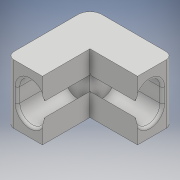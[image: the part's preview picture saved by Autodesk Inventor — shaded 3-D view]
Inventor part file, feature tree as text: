
AUTODESK INVENTOR PART (.ipt)
format: ipt  version: 2017 (Build 210142000, 142)  size: 176,640 bytes
history: native  units: mm
features: extrude x3, fillet x3, sketch x3
ambient origin geometry x8: Origin, YZ Plane, XZ Plane, XY Plane, X Axis, Y Axis, Z Axis, Center Point
bodies: Solid1 (feature_tree)
feature tree (9):
  extrude  "Extrusion1"  Depth=35.0mm
  extrude  "Extrusion9"  Depth=35.0mm
  extrude  "Extrusion10"  Depth=3.0mm
  fillet  "Fillet10"  Radius=16.4mm
  fillet  "Fillet11"  Radius=10.4mm
  fillet  "Fillet12"  Radius=20.0mm
  sketch  "Sketch1"  dims[d0=15.0mm d1=35.0mm]
  sketch  "Sketch15"  dims[d2=35.0mm d3=15.0mm]
  sketch  "Sketch16"  dims[d4=25.0mm d5=0.0mm d58=10.4mm d59=16.4mm d60=10.4mm d61=20.0mm d62=0.0mm d63=10.5mm d64=10.5mm d65=16.5mm d66=20.0mm d67=0.0mm d68=1.0mm d69=5.0mm d70=3.0mm]
